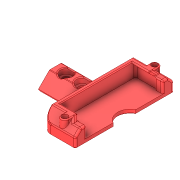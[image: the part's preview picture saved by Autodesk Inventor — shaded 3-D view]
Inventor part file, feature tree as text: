
AUTODESK INVENTOR PART (.ipt)
format: ipt  version: 2021 (Build 250183000, 183)  size: 696,832 bytes
history: native  units: mm
features: projected_geometry x15, fillet x6, extrude x5, sketch x5, other x4, direct_edit x3, chamfer x3, plane x1, mirror x1
ambient origin geometry x8: Origin, YZ Plane, XZ Plane, XY Plane, X Axis, Y Axis, Z Axis, Center Point
bodies: Volumenkörper1 (feature_tree), Body1 (feature_tree)
feature tree (43):
  extrude  "Extrusion1"  Depth=10.0mm
  extrude  "Extrusion4"  Depth=1.75mm TaperAngle=45.0deg
  direct_edit  "Direktbearbeitung2"
  direct_edit  "Direktbearbeitung3"
  direct_edit  "Direktbearbeitung4"
  chamfer  "Fase1"  Distance=1.0mm
  fillet  "Rundung7"  Radius=2.55mm
  fillet  "Rundung8"  Radius=2.0mm
  fillet  "Rundung9"  Radius=2.307107mm
  fillet  "Rundung10"  Radius=4.0mm
  extrude  "Extrusion6"  Depth=0.5mm
  chamfer  "Fase2"  Distance=10.0mm
  extrude  "Extrusion7"  Depth=1.0mm TaperAngle=45.0deg
  fillet  "Rundung11"  Radius=1.0mm
  fillet  "Rundung12"  Radius=2.0mm
  extrude  "Extrusion8"  Depth=0.5mm
  chamfer  "Fase3"  [1 undecoded]
  plane  "Arbeitsebene1"
  mirror  "Spiegeln1"
  sketch  "Skizze1"  dims[d0=10.0mm d1=0.0mm d17=1.75mm]
  projected_geometry  "Projizierte Kontur1"
  projected_geometry  "Projizierte Kontur2"
  projected_geometry  "Projizierte Kontur3"
  projected_geometry  "Projizierte Kontur4"
  sketch  "Skizze4"  dims[d18=0.0mm d19=0.0mm d20=1.75mm d21=2.0mm d22=45.0deg]
  projected_geometry  "Projizierte Kontur12"
  sketch  "Skizze5"  dims[d23=0.5mm]
  projected_geometry  "Projizierte Kontur13"
  projected_geometry  "Projizierte Kontur14"
  projected_geometry  "Projizierte Kontur15"
  projected_geometry  "Projizierte Kontur16"
  projected_geometry  "Projizierte Kontur17"
  projected_geometry  "Projizierte Kontur18"
  projected_geometry  "Projizierte Kontur19"
  projected_geometry  "Projizierte Kontur20"
  projected_geometry  "Projizierte Kontur21"
  sketch  "Skizze6"  dims[d24=0.55mm]
  sketch  "Skizze7"  dims[d25=1.0mm d26=1.0mm d27=2.55mm d28=2.0mm d29=2.307107mm d30=4.0mm d33=4.0mm d34=10.0mm d35=0.0mm d36=0.0929mm d37=1.0mm d38=45.0deg d39=1.0mm d40=0.0mm d41=2.0mm d42=0.5mm d43=0.0mm d44=0.0mm d45=2.0mm d46=0.2mm d47=45.0deg]
  projected_geometry  "Projizierte Kontur22"
  other  "Löschen4"
  other  "Löschen5"
  other  "Löschen6"
  other  "Löschen7"
note: 1 required parameter value undecoded (feature->parameter linkage not recoverable at this tier; creation-order binding heuristic only, values carry confidence <= 0.55)
